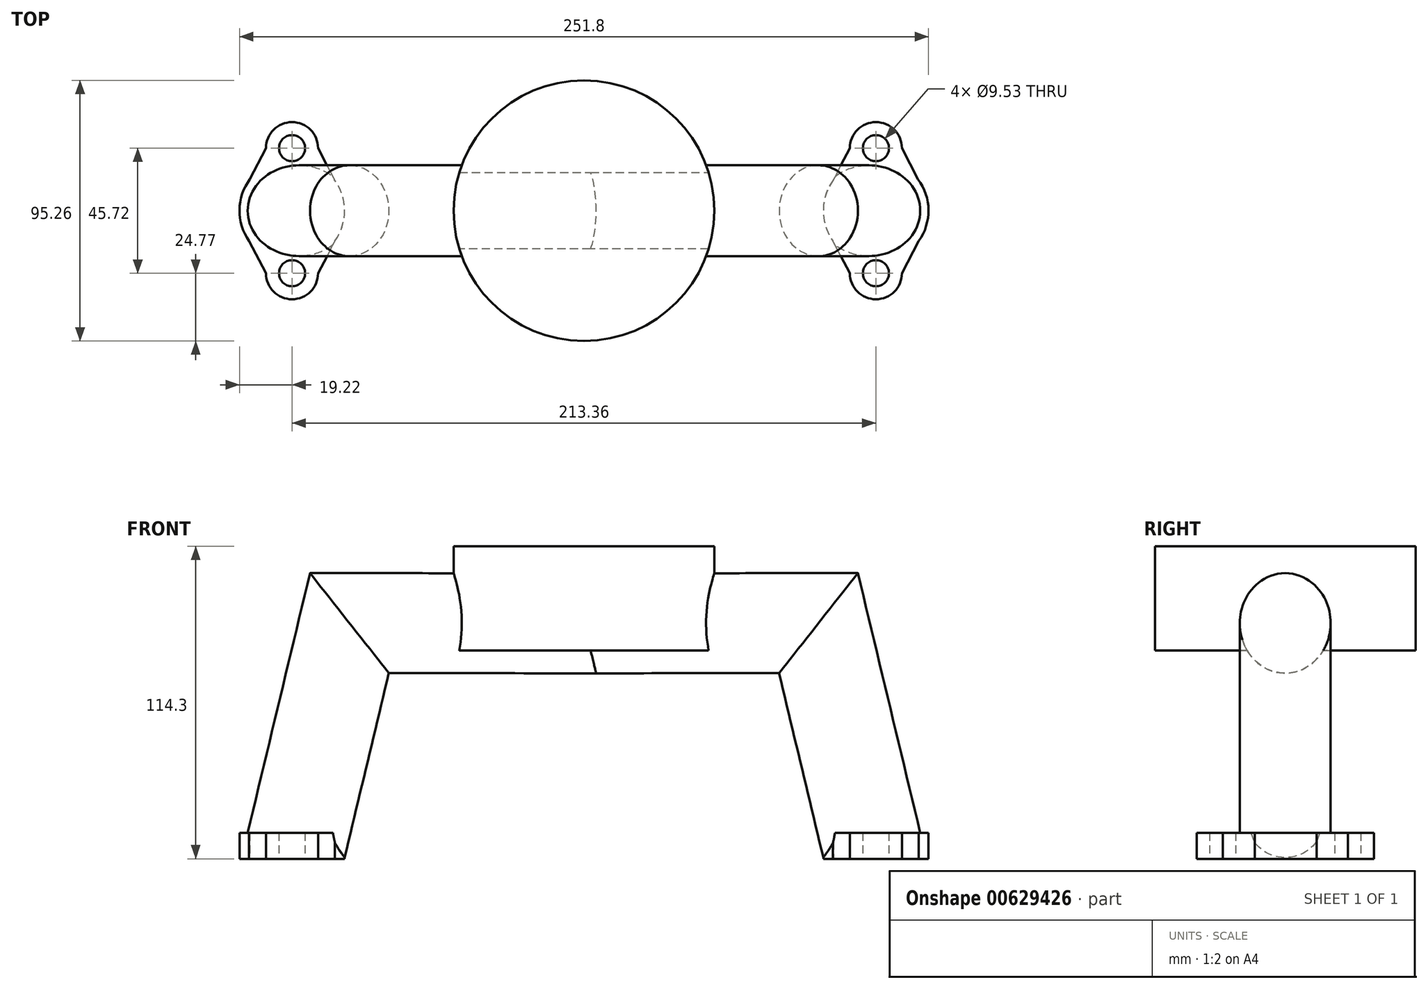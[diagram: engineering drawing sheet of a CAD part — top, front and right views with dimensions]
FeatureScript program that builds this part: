
annotation { "Feature Type Name" : "Feature", "Feature Type Description" : "" }
export const myFeature = defineFeature(function(context is Context, id is Id, definition is map)
    precondition{}
    {
        {
            var Q0;
            Q0=qCreatedBy(makeId("Top.planeOp"),FACE);
            var sketch = newSketch(context, id + "F0", { "sketchPlane" : qUnion([Q0])});
            skLineSegment(sketch, "E0", {"start": v(0, 0) * mm, "end": v(-106.68, 0) * mm, "construction": true});
            skLineSegment(sketch, "E1", {"start": v(0, 0) * mm, "end": v(106.68, 0) * mm, "construction": true});
            skCircle(sketch, "E2", {"center": v(-106.68, 0) * mm, "radius": 12.7 * mm});
            skCircle(sketch, "E3", {"center": v(106.68, 0) * mm, "radius": 12.7 * mm});
            skLineSegment(sketch, "E4", {"start": v(106.68, 0) * mm, "end": v(106.68, 22.86) * mm, "construction": true});
            skLineSegment(sketch, "E5", {"start": v(106.68, 0) * mm, "end": v(106.68, -22.86) * mm, "construction": true});
            skCircle(sketch, "E6", {"center": v(106.68, 22.86) * mm, "radius": 4.76 * mm});
            skCircle(sketch, "E7", {"center": v(106.68, -22.86) * mm, "radius": 4.76 * mm});
            skCircle(sketch, "E8", {"center": v(-106.68, 22.86) * mm, "radius": 4.76 * mm});
            skCircle(sketch, "E9", {"center": v(-106.68, -22.86) * mm, "radius": 4.76 * mm});
            skArc(sketch, "E10", {"start": v(-97.16, 22.86) * mm, "mid": v(-106.68, 32.39) * mm, "end": v(-116.2, 22.86) * mm});
            skArc(sketch, "E11", {"start": v(-116.2, -22.86) * mm, "mid": v(-106.68, -32.38) * mm, "end": v(-97.16, -22.86) * mm});
            skLineSegment(sketch, "E12", {"start": v(-116.2, 22.86) * mm, "end": v(-122.1, 11.48) * mm});
            skLineSegment(sketch, "E13", {"start": v(-116.2, -22.86) * mm, "end": v(-122.38, -11.09) * mm});
            skLineSegment(sketch, "E14", {"start": v(-106.68, 0) * mm, "end": v(-106.68, 5.3) * mm, "construction": true});
            skLineSegment(sketch, "E15.MirrorCS", {"start": v(-97.15, 22.86) * mm, "end": v(-91.27, 11.48) * mm});
            skLineSegment(sketch, "E16.MirrorCS", {"start": v(-97.16, -22.86) * mm, "end": v(-90.98, -11.09) * mm});
            skArc(sketch, "E17.trimOffspring", {"start": v(-122.1, 11.48) * mm, "mid": v(-125.9, 0.24) * mm, "end": v(-122.38, -11.09) * mm});
            skArc(sketch, "E18.trimOffspring", {"start": v(-90.98, -11.09) * mm, "mid": v(-87.47, 0.24) * mm, "end": v(-91.27, 11.48) * mm});
            skArc(sketch, "E19.MirrorCS", {"start": v(90.98, -11.09) * mm, "mid": v(87.47, 0.24) * mm, "end": v(91.27, 11.48) * mm});
            skLineSegment(sketch, "E20.MirrorCS", {"start": v(97.15, 22.86) * mm, "end": v(91.27, 11.48) * mm});
            skArc(sketch, "E21.MirrorCS", {"start": v(97.16, 22.86) * mm, "mid": v(106.68, 32.39) * mm, "end": v(116.2, 22.86) * mm});
            skLineSegment(sketch, "E22.MirrorCS", {"start": v(116.2, 22.86) * mm, "end": v(122.1, 11.48) * mm});
            skArc(sketch, "E23.MirrorCS", {"start": v(122.1, 11.48) * mm, "mid": v(125.9, 0.24) * mm, "end": v(122.38, -11.09) * mm});
            skLineSegment(sketch, "E24.MirrorCS", {"start": v(116.2, -22.86) * mm, "end": v(122.38, -11.09) * mm});
            skArc(sketch, "E25.MirrorCS", {"start": v(116.2, -22.86) * mm, "mid": v(106.68, -32.38) * mm, "end": v(97.16, -22.86) * mm});
            skLineSegment(sketch, "E26.MirrorCS", {"start": v(97.16, -22.86) * mm, "end": v(90.98, -11.09) * mm});
            skCircle(sketch, "E27", {"center": v(0, 0) * mm, "radius": 47.63 * mm});
            skSolve(sketch);
        }
        {
            var Q0;
            Q0=qCreatedBy(makeId("Front.planeOp"),FACE);
            var sketch = newSketch(context, id + "F1", { "sketchPlane" : qUnion([Q0])});
            skFitSpline(sketch, "E28", {"points": [v(-106.68, 0) * mm, v(-104.8, 15.4) * mm, v(-101.49, 19.82) * mm, v(-74.94, 33.64) * mm, v(-45.81, 42.5) * mm, v(0, 44.34) * mm, v(0, 44.52) * mm], "startDerivative": vector(8.79, 112.78) * mm, "endDerivative": vector(-6.15, 10.89) * mm});
            skFitSpline(sketch, "E29", {"points": [v(0.1, 44.52) * mm, v(0.04, 44.46) * mm], "startDerivative": vector(-0.06, -0.06) * mm, "endDerivative": vector(-0.06, -0.06) * mm});
            skLineSegment(sketch, "E30", {"start": v(-106.68, 0) * mm, "end": v(-85.93, 86.44) * mm});
            skLineSegment(sketch, "E31", {"start": v(-85.93, 86.44) * mm, "end": v(0, 86.39) * mm});
            skLineSegment(sketch, "E32.MirrorCS", {"start": v(85.93, 86.44) * mm, "end": v(0, 86.39) * mm});
            skLineSegment(sketch, "E33.MirrorCS", {"start": v(106.68, 0) * mm, "end": v(85.93, 86.44) * mm});
            skFitSpline(sketch, "E34.trimOffspring", {"points": [v(106.68, 0) * mm, v(104.8, 15.4) * mm, v(101.49, 19.82) * mm, v(74.94, 33.64) * mm, v(45.81, 42.5) * mm, v(0, 44.34) * mm, v(0, 44.52) * mm], "startDerivative": vector(-8.79, 112.78) * mm, "endDerivative": vector(6.15, 10.89) * mm});
            skSolve(sketch);
        }
        {
            var Q0;
            Q0=qCreatedBy(makeId("Top.planeOp"),FACE);
            var sketch = newSketch(context, id + "F2", { "sketchPlane" : qUnion([Q0])});
            skEllipse(sketch, "E35", {"center": v(-106.38, 0) * mm, "majorRadius": 18.8 * mm, "minorRadius": 16.6 * mm, "majorAxis": v(-1, 0)});
            skSolve(sketch);
        }
        {
            var Q0;
            Q0 = qSketchRegion(id + "F2", true);
            var Q1;
            Q1=sQuery(id+"F1.wireOp",EDGE,"E30");
            var Q2;
            Q2=sQuery(id+"F1.wireOp",EDGE,"E31");
            sweep(context, id + "F3", {"profiles" : qUnion([Q0]), "path" : qUnion([Q1, Q2])});
        }
        {
            var Q0;
            Q0=makeQuery(id+"F3.opSweep","SWEPT_BODY",BODY,{"disambiguationData":[OSD([sQuery(id+"F1.wireOp",EDGE,"E31"),sQuery(id+"F2.wireOp",EDGE,"E35")])]});
            var Q1;
            Q1=qCreatedBy(makeId("Right.planeOp"),FACE);
            mirror(context, id + "F4", {"operationType" : NewBodyOperationType.ADD, "entities" : qUnion([Q0]), "mirrorPlane" : qUnion([Q1])});
        }
        {
            var Q0;
            Q0=makeQuery(id+"F0.imprint","IMPRINT",FACE,{"disambiguationData":[TD([[makeQuery(id+"F0.imprint","IMPRINT",EDGE,{"derivedFrom":sQuery(id+"F0.wireOp",EDGE,"E27")}),1.0]])]});
            extrude(context, id + "F5", {"entities" : qUnion([Q0]), "operationType" : NewBodyOperationType.ADD, "depth" : 114.3 * mm, "offsetDistance" : 25.4 * mm, "hasSecondDirection" : true, "secondDirectionOppositeDirection" : false, "secondDirectionDepth" : 76.2 * mm});
        }
        {
            var Q0;
            Q0=makeQuery(id+"F0.imprint","IMPRINT",FACE,{"disambiguationData":[TD([[makeQuery(id+"F0.imprint","IMPRINT",EDGE,{"derivedFrom":sQuery(id+"F0.wireOp",EDGE,"E3")}),-1.0]])]});
            var Q1;
            Q1=makeQuery(id+"F0.imprint","IMPRINT",FACE,{"disambiguationData":[TD([[makeQuery(id+"F0.imprint","IMPRINT",EDGE,{"derivedFrom":sQuery(id+"F0.wireOp",EDGE,"E2")}),-1.0]])]});
            extrude(context, id + "F6", {"entities" : qUnion([Q0, Q1]), "operationType" : NewBodyOperationType.ADD, "depth" : 9.52 * mm, "offsetDistance" : 25.4 * mm});
        }
    });
